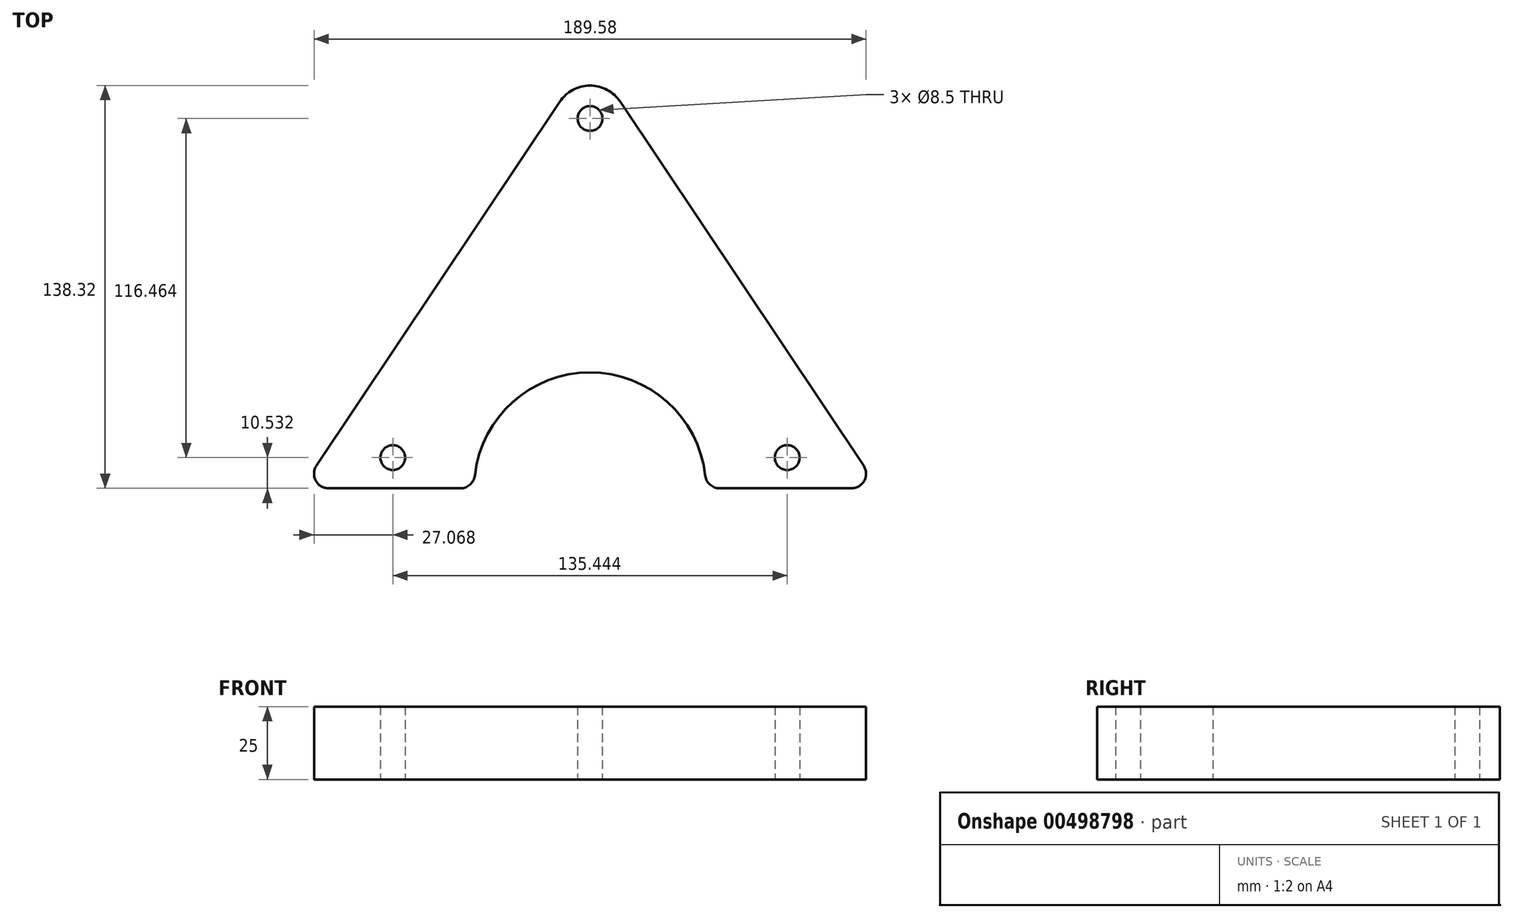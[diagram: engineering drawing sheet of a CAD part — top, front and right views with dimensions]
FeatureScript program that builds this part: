
annotation { "Feature Type Name" : "Feature", "Feature Type Description" : "" }
export const myFeature = defineFeature(function(context is Context, id is Id, definition is map)
    precondition{}
    {
        {
            var Q0;
            Q0=qCreatedBy(makeId("Top.planeOp"),FACE);
            var sketch = newSketch(context, id + "F0", { "sketchPlane" : qUnion([Q0])});
            skLineSegment(sketch, "E0", {"start": v(-99.14, -54.8) * mm, "end": v(0, 93.52) * mm});
            skLineSegment(sketch, "E1", {"start": v(-99.14, -54.8) * mm, "end": v(-39.8, -54.8) * mm});
            skArc(sketch, "E2", {"start": v(0, -15.01) * mm, "mid": v(-28.14, -26.67) * mm, "end": v(-39.8, -54.8) * mm});
            skLineSegment(sketch, "E3.MirrorCS", {"start": v(99.14, -54.8) * mm, "end": v(0, 93.52) * mm});
            skLineSegment(sketch, "E4.MirrorCS", {"start": v(99.14, -54.8) * mm, "end": v(39.8, -54.8) * mm});
            skArc(sketch, "E5.MirrorCS", {"start": v(0, -15.01) * mm, "mid": v(28.14, -26.67) * mm, "end": v(39.8, -54.8) * mm});
            skPoint(sketch, "E6.MirrorC.center.orphan", {"position": v(0, 98.44) * mm});
            skCircle(sketch, "E7", {"center": v(0, 72.2) * mm, "radius": 4.25 * mm});
            skCircle(sketch, "E8", {"center": v(-67.72, -44.27) * mm, "radius": 4.25 * mm});
            skCircle(sketch, "E9.MirrorC", {"center": v(67.72, -44.27) * mm, "radius": 4.25 * mm});
            skPoint(sketch, "E10.MirrorCS.start.orphan", {"position": v(-3.3, 98.44) * mm});
            skPoint(sketch, "E11.trimOffspring.start.orphan", {"position": v(3.3, 98.44) * mm});
            skSolve(sketch);
        }
        {
            var Q0;
            Q0=makeQuery(id+"F0.imprint","IMPRINT",FACE,{"disambiguationData":[TD([[makeQuery(id+"F0.imprint","IMPRINT",EDGE,{"derivedFrom":sQuery(id+"F0.wireOp",EDGE,"E0")}),-1.0]])]});
            extrude(context, id + "F1", {"entities" : qUnion([Q0]), "depth" : 25 * mm});
        }
        {
            var Q0;
            Q0=makeQuery(id+"F1.opExtrude","SWEPT_EDGE",EDGE,{"disambiguationData":[OSD([sQuery(id+"F0.wireOp",EDGE,"E0"),sQuery(id+"F0.wireOp",EDGE,"E3.MirrorCS")])]});
            fillet(context, id + "F2", {"entities" : qUnion([Q0]), "radius" : 12.5 * mm, "tangentPropagation" : true, "allowEdgeOverflow" : false});
        }
        {
            var Q0;
            Q0=makeQuery(id+"F1.opExtrude","SWEPT_EDGE",EDGE,{"disambiguationData":[OSD([sQuery(id+"F0.wireOp",EDGE,"E1"),sQuery(id+"F0.wireOp",EDGE,"E2")])]});
            var Q1;
            Q1=makeQuery(id+"F1.opExtrude","SWEPT_EDGE",EDGE,{"disambiguationData":[OSD([sQuery(id+"F0.wireOp",EDGE,"E4.MirrorCS"),sQuery(id+"F0.wireOp",EDGE,"E5.MirrorCS")])]});
            var Q2;
            Q2=makeQuery(id+"F1.opExtrude","SWEPT_EDGE",EDGE,{"disambiguationData":[OSD([sQuery(id+"F0.wireOp",EDGE,"E3.MirrorCS"),sQuery(id+"F0.wireOp",EDGE,"E4.MirrorCS")])]});
            var Q3;
            Q3=makeQuery(id+"F1.opExtrude","SWEPT_EDGE",EDGE,{"disambiguationData":[OSD([sQuery(id+"F0.wireOp",EDGE,"E0"),sQuery(id+"F0.wireOp",EDGE,"E1")])]});
            fillet(context, id + "F3", {"entities" : qUnion([Q0, Q1, Q2, Q3]), "radius" : 5 * mm, "tangentPropagation" : true, "allowEdgeOverflow" : false});
        }
    });
